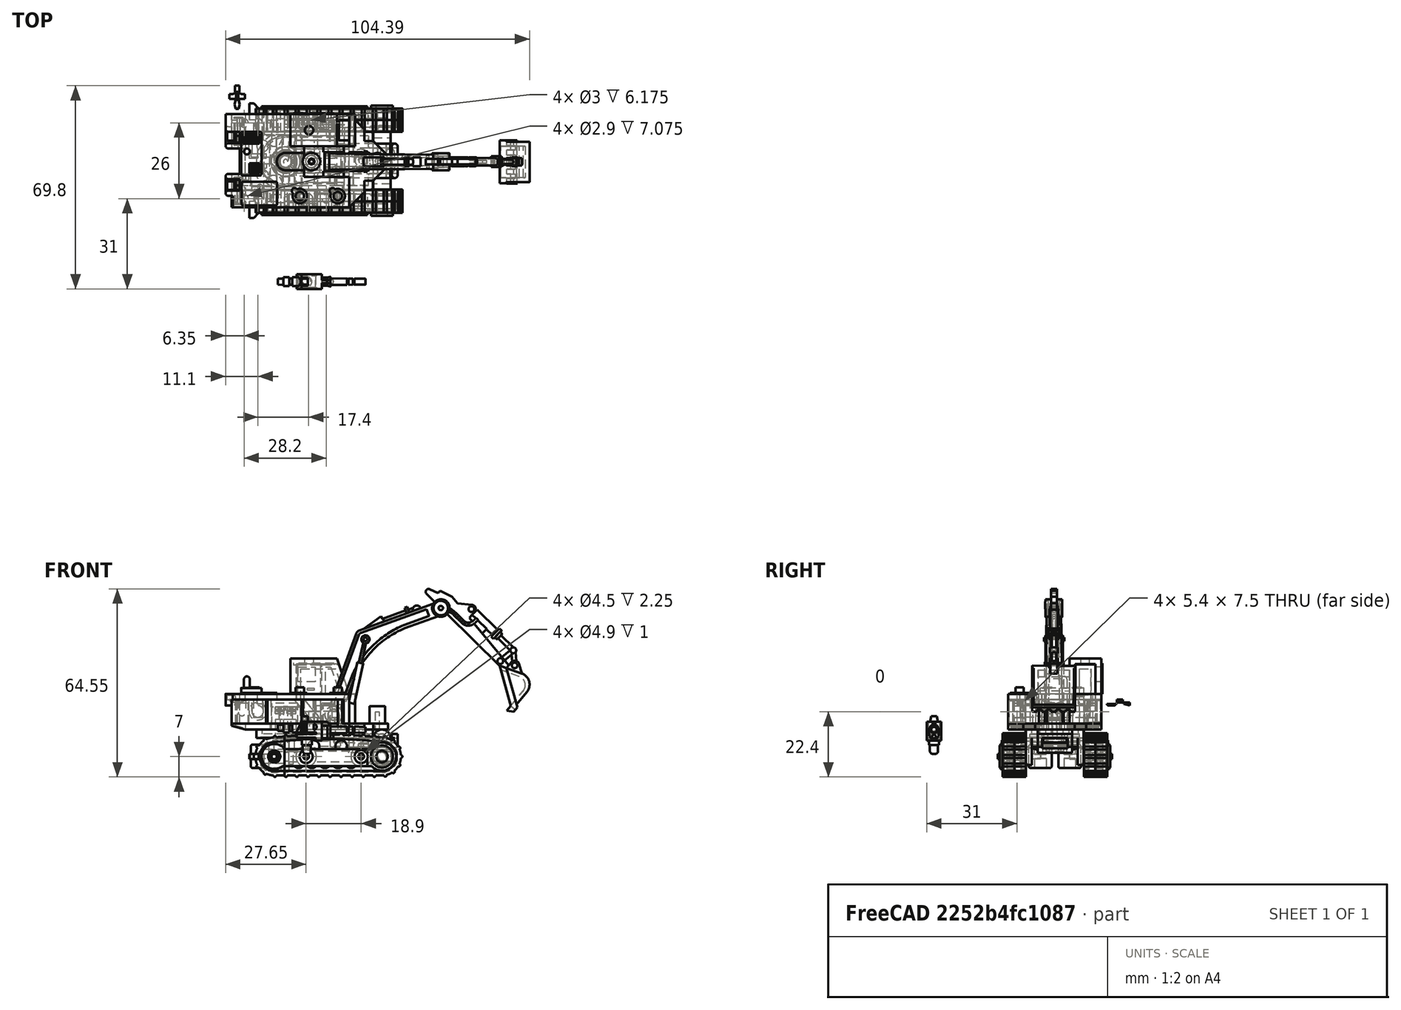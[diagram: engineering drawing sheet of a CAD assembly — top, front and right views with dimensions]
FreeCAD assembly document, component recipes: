
FREECAD ASSEMBLY — COMPONENT RECIPES ("Scavanger")

This assembly document has 15 components, labeled P0..P14 below (a component is one placed body or linked part). 15 of them carry a construction recipe — the FreeCAD feature program that regenerates the part from scratch, quoted from this document or its linked companion documents; the rest are supplied as boundary geometry only. No exploded tour is included for this assembly.
NOTE — document 4 of 4 of this assembly tour. The two overview renders and the header above are repeated from document 1; the component sections below continue where the previous document stopped.
COMPONENT P14 — recipe-attached ("Head", modeled in this document).
Construction recipe (the document's own serialized feature program — sketch geometry with constraints, then the solid features built on it; lengths are millimeters unless a unit is written):

FEATURE [Sketcher::SketchObject] Sketch213
  ArcFitTolerance = 1e-06
  AttachmentSupport = -> [XY_Plane011]
  FullyConstrained = true
  MakeInternals = false
  MapMode = 5
  sketch-geometry (4):
    g0: LineSegment StartX=0 StartY=0 StartZ=0 EndX=7.9 EndY=0 EndZ=0
    g1: LineSegment StartX=7.9 StartY=0 StartZ=0 EndX=7.9 EndY=9.8 EndZ=0
    g2: LineSegment StartX=7.9 StartY=9.8 StartZ=0 EndX=0 EndY=9.8 EndZ=0
    g3: LineSegment StartX=0 StartY=9.8 StartZ=0 EndX=0 EndY=0 EndZ=0
  constraints (11):
    c: Coincident(g0,g1)
    c: Coincident(g1,g2)
    c: Coincident(g2,g3)
    c: Coincident(g3,g0)
    c: Horizontal(g0)
    c: Horizontal(g2)
    c: Vertical(g1)
    c: Vertical(g3)
    c: Coincident(g0,g-1)
    c: DistanceX(g0,g0) = 7.9
    c: DistanceY(g1,g1) = 9.8
FEATURE [PartDesign::Pad] Pad137
  Direction = (0,0,1)
  Length = 2.75
  Length2 = 10
  Profile = -> Sketch213
  ReferenceAxis = -> Sketch213 [N_Axis]
  Refine = true
  Suppressed = false
  Type = 0
FEATURE [Sketcher::SketchObject] Sketch214
  ArcFitTolerance = 1e-06
  AttachmentSupport = -> [Pad137]
  ExternalGeometry = -> [Pad137]
  FullyConstrained = true
  MakeInternals = false
  MapMode = 5
  Placement = pos=(0,0,0) rot=(1,0,0;3.14159rad)
  sketch-geometry (4):
    g0: LineSegment StartX=0 StartY=0 StartZ=0 EndX=0 EndY=-1.4 EndZ=0
    g1: LineSegment StartX=0 StartY=-1.4 StartZ=0 EndX=7.9 EndY=-1.4 EndZ=0
    g2: LineSegment StartX=7.9 StartY=-1.4 StartZ=0 EndX=7.9 EndY=0 EndZ=0
    g3: LineSegment StartX=7.9 StartY=0 StartZ=0 EndX=0 EndY=0 EndZ=0
  constraints (11):
    c: Coincident(g0,g1)
    c: Coincident(g1,g2)
    c: Coincident(g2,g3)
    c: Coincident(g3,g0)
    c: Vertical(g0)
    c: Vertical(g2)
    c: Horizontal(g1)
    c: Horizontal(g3)
    c: Coincident(g0,g-1)
    c: PointOnObject(g1,g-3)
    c: DistanceY(g2,g2) = 1.4
FEATURE [PartDesign::Pad] Pad138
  BaseFeature = -> Pad137
  Direction = (0,0,-1)
  Length = 2
  Length2 = 10
  Profile = -> Sketch214
  ReferenceAxis = -> Sketch214 [N_Axis]
  Refine = true
  Suppressed = false
  Type = 0
FEATURE [Sketcher::SketchObject] Sketch215
  ArcFitTolerance = 1e-06
  AttachmentSupport = -> [Pad138]
  ExternalGeometry = -> [Pad138]
  FullyConstrained = true
  MakeInternals = false
  MapMode = 5
  Placement = pos=(0,0,0) rot=(0.57735,-0.57735,-0.57735;2.0944rad)
  sketch-geometry (1):
    g0: Circle CenterX=-8.5 CenterY=0 CenterZ=0 NormalX=0 NormalY=0 NormalZ=1 AngleXU=0 Radius=1.3
  constraints (3):
    c: Diameter(g0) = 2.6
    c: PointOnObject(g0,g-4)
    c: PointOnObject(g-4,g0)
FEATURE [PartDesign::Pad] Pad139
  BaseFeature = -> Pad138
  Direction = (-1,0,0)
  Length = 1.6
  Length2 = 10
  Profile = -> Sketch215
  ReferenceAxis = -> Sketch215 [N_Axis]
  Refine = true
  Suppressed = false
  Type = 0
FEATURE [PartDesign::Pad] Pad140
  BaseFeature = -> Pad139
  Direction = (-1,0,0)
  Length = 9.5
  Length2 = 10
  Profile = -> Sketch215
  ReferenceAxis = -> Sketch215 [N_Axis]
  Refine = true
  Reversed = true
  Suppressed = false
  Type = 0
FEATURE [Sketcher::SketchObject] Sketch216
  ArcFitTolerance = 1e-06
  AttachmentSupport = -> [Pad140]
  ExternalGeometry = -> [Pad140]
  FullyConstrained = true
  MakeInternals = false
  MapMode = 5
  Placement = pos=(0,0,0) rot=(0.57735,-0.57735,-0.57735;2.0944rad)
  sketch-geometry (4):
    g0: LineSegment StartX=-6.9 StartY=2.75 StartZ=0 EndX=-6.9 EndY=0 EndZ=0
    g1: LineSegment StartX=-6.9 StartY=0 StartZ=0 EndX=-5.4 EndY=0 EndZ=0
    g2: LineSegment StartX=-5.4 StartY=0 StartZ=0 EndX=-5.4 EndY=2.75 EndZ=0
    g3: LineSegment StartX=-5.4 StartY=2.75 StartZ=0 EndX=-6.9 EndY=2.75 EndZ=0
  constraints (12):
    c: Coincident(g0,g1)
    c: Coincident(g1,g2)
    c: Coincident(g2,g3)
    c: Coincident(g3,g0)
    c: Vertical(g0)
    c: Vertical(g2)
    c: Horizontal(g1)
    c: Horizontal(g3)
    c: PointOnObject(g0,g-3)
    c: PointOnObject(g1,g-4)
    c: DistanceX(g1,g1) = 1.5
    c: DistanceX(g-3,g0) = 2.9
FEATURE [PartDesign::Pad] Pad141
  BaseFeature = -> Pad140
  Direction = (-1,0,0)
  Length = 0.45
  Length2 = 10
  Profile = -> Sketch216
  ReferenceAxis = -> Sketch216 [N_Axis]
  Refine = true
  Suppressed = false
  Type = 0
FEATURE [Sketcher::SketchObject] Sketch217
  ArcFitTolerance = 1e-06
  AttachmentSupport = -> [Pad141]
  ExternalGeometry = -> [Pad141]
  FullyConstrained = true
  MakeInternals = false
  MapMode = 5
  Placement = pos=(7.9,0,0) rot=(0.57735,0.57735,0.57735;2.0944rad)
  sketch-geometry (4):
    g0: LineSegment StartX=5.4 StartY=2.75 StartZ=0 EndX=5.4 EndY=0 EndZ=0
    g1: LineSegment StartX=5.4 StartY=0 StartZ=0 EndX=6.9 EndY=0 EndZ=0
    g2: LineSegment StartX=6.9 StartY=0 StartZ=0 EndX=6.9 EndY=2.75 EndZ=0
    g3: LineSegment StartX=6.9 StartY=2.75 StartZ=0 EndX=5.4 EndY=2.75 EndZ=0
  constraints (10):
    c: Coincident(g0,g1)
    c: Coincident(g1,g2)
    c: Coincident(g2,g3)
    c: Coincident(g3,g0)
    c: Vertical(g0)
    c: Vertical(g2)
    c: Horizontal(g1)
    c: Horizontal(g3)
    c: Coincident(g0,g-3)
    c: Coincident(g1,g-4)
FEATURE [PartDesign::Pad] Pad142
  BaseFeature = -> Pad141
  Direction = (1,0,0)
  Length = 0.45
  Length2 = 10
  Profile = -> Sketch217
  ReferenceAxis = -> Sketch217 [N_Axis]
  Refine = true
  Suppressed = false
  Type = 0
FEATURE [PartDesign::Chamfer] Chamfer003
  Angle = 45
  Base = -> Pad142 [Edge47,Edge45,Edge16,Edge18]
  BaseFeature = -> Pad142
  ChamferType = 0
  FlipDirection = false
  Refine = true
  Size = 0.4
  Size2 = 1
  SupportTransform = false
  Suppressed = false
  UseAllEdges = false
FEATURE [Sketcher::SketchObject] Sketch218
  ArcFitTolerance = 1e-06
  AttachmentSupport = -> [Chamfer003]
  ExternalGeometry = -> [Chamfer003]
  FullyConstrained = true
  MakeInternals = false
  MapMode = 5
  Placement = pos=(0,0,2.75) rot=(0,0,1;0rad)
  sketch-geometry (1):
    g0: Circle CenterX=3.95 CenterY=4.9 CenterZ=0 NormalX=0 NormalY=0 NormalZ=1 AngleXU=0 Radius=2.45
  constraints (5):
    c: Diameter(g0) = 4.9
    c: DistanceX(g-3,g-3) = 7.9
    c: DistanceY(g-4,g-3) = 9.8
    c: DistanceX(g0,g-4) = 3.95
    c: DistanceY(g-4,g0) = 4.9
FEATURE [PartDesign::Pocket] Pocket098
  BaseFeature = -> Chamfer003
  Direction = (0,0,-1)
  Length = 1.7
  Length2 = 5
  Profile = -> Sketch218
  ReferenceAxis = -> Sketch218 [N_Axis]
  Refine = true
  Suppressed = false
  Type = 0
FEATURE [Sketcher::SketchObject] Sketch219
  ArcFitTolerance = 1e-06
  AttachmentOffset = pos=(0,0,-1) rot=(0,0,1;0rad)
  AttachmentSupport = -> [Pocket098]
  ExternalGeometry = -> [Pocket098]
  FullyConstrained = true
  MakeInternals = false
  MapMode = 5
  Placement = pos=(1,0,0) rot=(0.57735,-0.57735,-0.57735;2.0944rad)
  sketch-geometry (5):
    g0: ArcOfCircle CenterX=-7.19261 CenterY=0.257783 CenterZ=0 NormalX=0 NormalY=0 NormalZ=1 AngleXU=0 Radius=4.5 StartAngle=5.75759 EndAngle=6.22587
    g1: LineSegment [constr] StartX=-1.4 StartY=-2 StartZ=0 EndX=-3.3 EndY=-2 EndZ=0
    g2: LineSegment StartX=-3.3 StartY=-2 StartZ=0 EndX=-5.26914 EndY=-1.65 EndZ=0
    g3: ArcOfCircle CenterX=-12.6824 CenterY=-0.512926 CenterZ=0 NormalX=0 NormalY=0 NormalZ=1 AngleXU=0 Radius=7.5 StartAngle=6.13099 EndAngle=6.35163
    g4: LineSegment StartX=-5.2 StartY=-1.3e-15 StartZ=0 EndX=-2.7 EndY=1.6e-15 EndZ=0
  constraints (16):
    c: PointOnObject(g0,g-3)
    c: DistanceX(g0,g-3) = 1.3
    c: Coincident(g1,g-4)
    c: Coincident(g1,g0)
    c: Horizontal(g1)
    c: Coincident(g2,g0)
    c: Coincident(g3,g2)
    c: PointOnObject(g3,g-3)
    c: Coincident(g4,g3)
    c: Coincident(g4,g0)
    c: DistanceX(g3,g0) = 2.5
    c: Distance(g2) = 2
    c: DistanceX(g0,g0) = 0.6
    c: Radius(g0) = 4.5
    c: Radius(g3) = 7.5
    c: DistanceY(g0,g2) = 0.35
FEATURE [PartDesign::Pad] Pad143
  BaseFeature = -> Pocket098
  Direction = (-1,0,0)
  Length = 5.9
  Length2 = 10
  Profile = -> Sketch219
  ReferenceAxis = -> Sketch219 [N_Axis]
  Refine = true
  Reversed = true
  Suppressed = false
  Type = 0
FEATURE [Sketcher::SketchObject] Sketch220
  ArcFitTolerance = 1e-06
  AttachmentSupport = -> [Pad143]
  ExternalGeometry = -> [Pad143]
  FullyConstrained = true
  MakeInternals = false
  MapMode = 5
  Placement = pos=(1,0,0) rot=(0.57735,-0.57735,-0.57735;2.0944rad)
  sketch-geometry (4):
    g0: ArcOfCircle CenterX=-7.19261 CenterY=0.257783 CenterZ=0 NormalX=0 NormalY=0 NormalZ=1 AngleXU=0 Radius=4.5 StartAngle=5.85761 EndAngle=6.22587
    g1: LineSegment StartX=-3.094 StartY=-1.6 StartZ=0 EndX=-1.6 EndY=-0.737441 EndZ=0
    g2: LineSegment StartX=-1.6 StartY=-0.737441 StartZ=0 EndX=-1.6 EndY=0 EndZ=0
    g3: LineSegment StartX=-2.7 StartY=1.6e-15 StartZ=0 EndX=-1.6 EndY=0 EndZ=0
  constraints (11):
    c: PointOnObject(g0,g-3)
    c: Tangent(g0,g-3) = -1.5708
    c: DistanceY(g0,g0) = 1.6
    c: Coincident(g1,g0)
    c: Coincident(g2,g1)
    c: PointOnObject(g2,g-4)
    c: Vertical(g2)
    c: Coincident(g3,g0)
    c: Coincident(g3,g2)
    c: DistanceX(g3,g3) = 1.1
    c: Angle(g2,g1) = 2.0944
FEATURE [PartDesign::Pad] Pad144
  BaseFeature = -> Pad143
  Direction = (-1,0,0)
  Length = 5.9
  Length2 = 10
  Profile = -> Sketch220
  ReferenceAxis = -> Sketch220 [N_Axis]
  Refine = true
  Reversed = true
  Suppressed = false
  Type = 0
FEATURE [Sketcher::SketchObject] Sketch221
  ArcFitTolerance = 1e-06
  AttachmentSupport = -> [Pad144]
  ExternalGeometry = -> [Pad144]
  FullyConstrained = true
  MakeInternals = false
  MapMode = 5
  Placement = pos=(0,0,-2) rot=(1,0,0;3.14159rad)
  sketch-geometry (4):
    g0: LineSegment StartX=2.5 StartY=-1.6 StartZ=0 EndX=2.5 EndY=-3.094 EndZ=0
    g1: LineSegment StartX=2.5 StartY=-3.094 StartZ=0 EndX=5.4 EndY=-3.094 EndZ=0
    g2: LineSegment StartX=5.4 StartY=-3.094 StartZ=0 EndX=5.4 EndY=-1.6 EndZ=0
    g3: LineSegment StartX=5.4 StartY=-1.6 StartZ=0 EndX=2.5 EndY=-1.6 EndZ=0
  constraints (12):
    c: Coincident(g0,g1)
    c: Coincident(g1,g2)
    c: Coincident(g2,g3)
    c: Coincident(g3,g0)
    c: Vertical(g0)
    c: Vertical(g2)
    c: Horizontal(g1)
    c: Horizontal(g3)
    c: PointOnObject(g0,g-5)
    c: PointOnObject(g1,g-6)
    c: DistanceX(g-5,g0) = 1.5
    c: DistanceX(g2,g-5) = 1.5
FEATURE [PartDesign::Pocket] Pocket099
  BaseFeature = -> Pad144
  Direction = (0,0,1)
  Length = 2
  Length2 = 5
  Profile = -> Sketch221
  ReferenceAxis = -> Sketch221 [N_Axis]
  Refine = true
  Suppressed = false
  Type = 0
FEATURE [Sketcher::SketchObject] Sketch222
  ArcFitTolerance = 1e-06
  AttachmentSupport = -> [Pocket099]
  ExternalGeometry = -> [Pocket099]
  FullyConstrained = true
  MakeInternals = false
  MapMode = 5
  Placement = pos=(0,0,-2) rot=(1,0,0;3.14159rad)
  sketch-geometry (9):
    g0: LineSegment StartX=3.2 StartY=-1.6 StartZ=0 EndX=4.7 EndY=-1.6 EndZ=0
    g1: LineSegment StartX=4.7 StartY=-1.6 StartZ=0 EndX=5.075 EndY=-3.3 EndZ=0
    g2: LineSegment StartX=5.075 StartY=-3.3 StartZ=0 EndX=4.7 EndY=-5.26914 EndZ=0
    g3: LineSegment StartX=4.7 StartY=-5.26914 StartZ=0 EndX=3.2 EndY=-5.26914 EndZ=0
    g4: LineSegment StartX=3.2 StartY=-5.26914 StartZ=0 EndX=2.825 EndY=-3.3 EndZ=0
    g5: LineSegment StartX=2.825 StartY=-3.3 StartZ=0 EndX=3.2 EndY=-1.6 EndZ=0
    g6: LineSegment [constr] StartX=3.2 StartY=-1.6 StartZ=0 EndX=3.2 EndY=-5.26914 EndZ=0
    g7: LineSegment [constr] StartX=4.7 StartY=-1.6 StartZ=0 EndX=4.7 EndY=-5.26914 EndZ=0
    g8: LineSegment [constr] StartX=3.2 StartY=-1.6 StartZ=0 EndX=2.5 EndY=-1.6 EndZ=0
  constraints (26):
    c: Horizontal(g0)
    c: Coincident(g1,g0)
    c: PointOnObject(g1,g-8)
    c: Coincident(g2,g1)
    c: PointOnObject(g2,g-3)
    c: Coincident(g3,g2)
    c: PointOnObject(g3,g-3)
    c: Coincident(g4,g3)
    c: PointOnObject(g4,g-8)
    c: Coincident(g5,g4)
    c: Coincident(g5,g0)
    c: DistanceX(g0,g0) = 1.5
    c: DistanceX(g3,g3) = 1.5
    c: Coincident(g6,g0)
    c: Coincident(g6,g3)
    c: Vertical(g6)
    c: Coincident(g7,g0)
    c: Coincident(g7,g2)
    c: Coincident(g8,g0)
    c: Coincident(g8,g-6)
    c: Horizontal(g8)
    c: DistanceX(g4,g1) = 2.25
    c: DistanceX(g8,g-5) = 2.9
    c: DistanceX(g8,g0) = 0.7
    c: DistanceX(g-7,g4) = 0.325
    c: DistanceX(g1,g-7) = 0.325
FEATURE [PartDesign::Pad] Pad145
  BaseFeature = -> Pocket099
  Direction = (0,0,-1)
  Length = 2
  Length2 = 10
  Profile = -> Sketch222
  ReferenceAxis = -> Sketch222 [N_Axis]
  Refine = true
  Reversed = true
  Suppressed = false
  Type = 0
FEATURE [Sketcher::SketchObject] Sketch223
  ArcFitTolerance = 1e-06
  AttachmentSupport = -> [Pad145]
  ExternalGeometry = -> [Pad145]
  FullyConstrained = true
  MakeInternals = false
  MapMode = 5
  Placement = pos=(6.9,0,0) rot=(0.57735,0.57735,0.57735;2.0944rad)
  sketch-geometry (3):
    g0: LineSegment StartX=5.26914 StartY=-1.65 StartZ=0 EndX=5.26914 EndY=0 EndZ=0
    g1: LineSegment StartX=5.26914 StartY=0 StartZ=0 EndX=5.2 EndY=-1.3e-15 EndZ=0
    g2: ArcOfCircle CenterX=12.6825 CenterY=-0.512923 CenterZ=0 NormalX=0 NormalY=0 NormalZ=1 AngleXU=0 Radius=7.50006 StartAngle=3.07315 EndAngle=3.29379
  constraints (7):
    c: Coincident(g0,g-5)
    c: Coincident(g0,g-3)
    c: Coincident(g1,g0)
    c: Coincident(g1,g-5)
    c: Coincident(g2,g1)
    c: Coincident(g2,g0)
    c: Tangent(g2,g-5)
FEATURE [PartDesign::Pocket] Pocket100
  BaseFeature = -> Pad145
  Direction = (-1,0,0)
  Length = 5
  Length2 = 5
  Profile = -> Sketch223
  ReferenceAxis = -> Sketch223 [N_Axis]
  Refine = true
  Suppressed = false
  Type = 0
FEATURE [Sketcher::SketchObject] Sketch224
  ArcFitTolerance = 1e-06
  AttachmentSupport = -> [Pocket100]
  ExternalGeometry = -> [Pocket100]
  FullyConstrained = true
  MakeInternals = false
  MapMode = 5
  Placement = pos=(0,0,-2) rot=(1,0,0;3.14159rad)
  sketch-geometry (8):
    g0: LineSegment StartX=3.35588 StartY=-1.8 StartZ=0 EndX=4.54412 EndY=-1.8 EndZ=0
    g1: LineSegment StartX=4.54412 StartY=-1.8 StartZ=0 EndX=4.875 EndY=-3.3 EndZ=0
    g2: LineSegment StartX=4.875 StartY=-3.3 StartZ=0 EndX=4.53809 EndY=-5.06914 EndZ=0
    g3: LineSegment StartX=4.53809 StartY=-5.06914 StartZ=0 EndX=3.36191 EndY=-5.06914 EndZ=0
    g4: LineSegment StartX=3.36191 StartY=-5.06914 StartZ=0 EndX=3.025 EndY=-3.3 EndZ=0
    g5: LineSegment StartX=3.025 StartY=-3.3 StartZ=0 EndX=3.35588 EndY=-1.8 EndZ=0
    g6: LineSegment [constr] StartX=3.025 StartY=-3.3 StartZ=0 EndX=2.825 EndY=-3.3 EndZ=0
    g7: LineSegment [constr] StartX=4.875 StartY=-3.3 StartZ=0 EndX=5.075 EndY=-3.3 EndZ=0
  constraints (22):
    c: Horizontal(g0)
    c: Coincident(g1,g0)
    c: Coincident(g2,g1)
    c: Coincident(g3,g2)
    c: Horizontal(g3)
    c: Coincident(g4,g3)
    c: Coincident(g5,g4)
    c: Coincident(g5,g0)
    c: Parallel(g5,g-7)
    c: Parallel(g2,g-5)
    c: Parallel(g1,g-4)
    c: Parallel(g4,g-6)
    c: DistanceY(g0,g-7) = 0.2
    c: DistanceY(g-6,g3) = 0.2
    c: Coincident(g6,g4)
    c: Coincident(g6,g-7)
    c: Coincident(g7,g1)
    c: Coincident(g7,g-5)
    c: Horizontal(g6)
    c: Horizontal(g7)
    c: DistanceX(g6,g6) = 0.2
    c: DistanceX(g7,g7) = 0.2
FEATURE [PartDesign::Pocket] Pocket101
  BaseFeature = -> Pocket100
  Direction = (0,0,1)
  Length = 0.5
  Length2 = 5
  Profile = -> Sketch224
  ReferenceAxis = -> Sketch224 [N_Axis]
  Refine = true
  Suppressed = false
  Type = 0
FEATURE [Sketcher::SketchObject] Sketch225
  ArcFitTolerance = 1e-06
  AttachmentSupport = -> [Pocket101]
  ExternalGeometry = -> [Pocket101]
  FullyConstrained = true
  MakeInternals = false
  MapMode = 5
  Placement = pos=(0,0,-2) rot=(1,0,0;3.14159rad)
  sketch-geometry (4):
    g0: LineSegment StartX=3.2 StartY=-7.2 StartZ=0 EndX=3.2 EndY=-9.8 EndZ=0
    g1: LineSegment StartX=3.2 StartY=-9.8 StartZ=0 EndX=4.7 EndY=-9.8 EndZ=0
    g2: LineSegment StartX=4.7 StartY=-9.8 StartZ=0 EndX=4.7 EndY=-7.2 EndZ=0
    g3: LineSegment StartX=4.7 StartY=-7.2 StartZ=0 EndX=3.2 EndY=-7.2 EndZ=0
  constraints (13):
    c: Coincident(g0,g1)
    c: Coincident(g1,g2)
    c: Coincident(g2,g3)
    c: Coincident(g3,g0)
    c: Vertical(g0)
    c: Vertical(g2)
    c: Horizontal(g1)
    c: Horizontal(g3)
    c: PointOnObject(g0,g-3)
    c: PointOnObject(g1,g-4)
    c: DistanceX(g3,g3) = 1.5
    c: DistanceX(g-4,g-4) = 7.9
    c: DistanceX(g-3,g0) = 3.2
FEATURE [PartDesign::Pocket] Pocket102
  BaseFeature = -> Pocket101
  Direction = (0,0,1)
  Length = 1
  Length2 = 5
  Profile = -> Sketch225
  ReferenceAxis = -> Sketch225 [N_Axis]
  Refine = true
  Suppressed = false
  Type = 0
FEATURE [Sketcher::SketchObject] Sketch226
  ArcFitTolerance = 1e-06
  AttachmentSupport = -> [Pocket102]
  ExternalGeometry = -> [Pocket102]
  FullyConstrained = true
  MakeInternals = false
  MapMode = 5
  Placement = pos=(0,0,-2) rot=(1,0,0;3.14159rad)
  sketch-geometry (8):
    g0: LineSegment StartX=1.15 StartY=-7.2 StartZ=0 EndX=1.15 EndY=-9.8 EndZ=0
    g1: LineSegment StartX=1.15 StartY=-9.8 StartZ=0 EndX=1.95 EndY=-9.8 EndZ=0
    g2: LineSegment StartX=1.95 StartY=-9.8 StartZ=0 EndX=1.95 EndY=-7.2 EndZ=0
    g3: LineSegment StartX=1.95 StartY=-7.2 StartZ=0 EndX=1.15 EndY=-7.2 EndZ=0
    g4: LineSegment StartX=5.95 StartY=-7.2 StartZ=0 EndX=5.95 EndY=-9.8 EndZ=0
    g5: LineSegment StartX=5.95 StartY=-9.8 StartZ=0 EndX=6.75 EndY=-9.8 EndZ=0
    g6: LineSegment StartX=6.75 StartY=-9.8 StartZ=0 EndX=6.75 EndY=-7.2 EndZ=0
    g7: LineSegment StartX=6.75 StartY=-7.2 StartZ=0 EndX=5.95 EndY=-7.2 EndZ=0
  constraints (25):
    c: Coincident(g0,g1)
    c: Coincident(g1,g2)
    c: Coincident(g2,g3)
    c: Coincident(g3,g0)
    c: Vertical(g0)
    c: Vertical(g2)
    c: Horizontal(g1)
    c: Horizontal(g3)
    c: PointOnObject(g0,g-3)
    c: PointOnObject(g1,g-4)
    c: Coincident(g4,g5)
    c: Coincident(g5,g6)
    c: Coincident(g6,g7)
    c: Coincident(g7,g4)
    c: Vertical(g4)
    c: Vertical(g6)
    c: Horizontal(g5)
    c: Horizontal(g7)
    c: PointOnObject(g4,g-3)
    c: PointOnObject(g5,g-4)
    c: DistanceX(g3,g3) = 0.8
    c: DistanceX(g7,g7) = 0.8
    c: DistanceX(g-4,g-4) = 7.9
    c: DistanceX(g-4,g0) = 1.15
    c: DistanceX(g5,g-4) = 1.15
FEATURE [PartDesign::Pad] Pad146
  BaseFeature = -> Pocket102
  Direction = (0,0,-1)
  Length = 2
  Length2 = 10
  Profile = -> Sketch226
  ReferenceAxis = -> Sketch226 [N_Axis]
  Refine = true
  Reversed = true
  Suppressed = false
  Type = 0
FEATURE [Sketcher::SketchObject] Sketch227
  ArcFitTolerance = 1e-06
  AttachmentSupport = -> [Pad146]
  ExternalGeometry = -> [Pad146]
  FullyConstrained = true
  MakeInternals = false
  MapMode = 5
  Placement = pos=(0,0,-2) rot=(1,0,0;3.14159rad)
  sketch-geometry (4):
    g0: LineSegment StartX=3.2 StartY=-7.66934 StartZ=0 EndX=2.35 EndY=-7.2 EndZ=0
    g1: LineSegment StartX=2.35 StartY=-7.2 StartZ=0 EndX=5.55 EndY=-7.2 EndZ=0
    g2: LineSegment StartX=5.55 StartY=-7.2 StartZ=0 EndX=4.7 EndY=-7.66934 EndZ=0
    g3: LineSegment StartX=4.7 StartY=-7.66934 StartZ=0 EndX=3.2 EndY=-7.66934 EndZ=0
  constraints (10):
    c: Coincident(g0,g-4)
    c: PointOnObject(g0,g-3)
    c: Coincident(g1,g0)
    c: PointOnObject(g1,g-3)
    c: Coincident(g2,g1)
    c: Coincident(g2,g-4)
    c: Coincident(g3,g2)
    c: Coincident(g3,g0)
    c: DistanceX(g-3,g0) = 0.4
    c: DistanceX(g1,g-3) = 0.4
FEATURE [PartDesign::Pocket] Pocket103
  BaseFeature = -> Pad146
  Direction = (0,0,1)
  Length = 2
  Length2 = 5
  Profile = -> Sketch227
  ReferenceAxis = -> Sketch227 [N_Axis]
  Refine = true
  Suppressed = false
  Type = 0
FEATURE [Sketcher::SketchObject] Sketch228
  ArcFitTolerance = 1e-06
  AttachmentSupport = -> [Pocket103]
  ExternalGeometry = -> [Pocket103]
  FullyConstrained = true
  MakeInternals = false
  MapMode = 5
  Placement = pos=(0,0,0) rot=(1,0,0;3.14159rad)
  sketch-geometry (16):
    g0: LineSegment StartX=3.27732 StartY=-7.36934 StartZ=0 EndX=2.42732 EndY=-6.9 EndZ=0
    g1: LineSegment StartX=3.27732 StartY=-7.36934 StartZ=0 EndX=4.62268 EndY=-7.36934 EndZ=0
    g2: LineSegment StartX=4.62268 StartY=-7.36934 StartZ=0 EndX=5.47268 EndY=-6.9 EndZ=0
    g3: LineSegment StartX=5.47268 StartY=-6.9 StartZ=0 EndX=6.9 EndY=-6.9 EndZ=0
    g4: LineSegment StartX=6.9 StartY=-6.9 StartZ=0 EndX=6.9 EndY=-7.2 EndZ=0
    g5: LineSegment StartX=6.9 StartY=-7.2 StartZ=0 EndX=5.55 EndY=-7.2 EndZ=0
    g6: LineSegment StartX=5.55 StartY=-7.2 StartZ=0 EndX=4.7 EndY=-7.66934 EndZ=0
    g7: LineSegment StartX=4.7 StartY=-7.66934 StartZ=0 EndX=3.2 EndY=-7.66934 EndZ=0
    g8: LineSegment StartX=3.2 StartY=-7.66934 StartZ=0 EndX=2.35 EndY=-7.2 EndZ=0
    g9: LineSegment StartX=2.35 StartY=-7.2 StartZ=0 EndX=1 EndY=-7.2 EndZ=0
    g10: LineSegment StartX=1 StartY=-7.2 StartZ=0 EndX=1 EndY=-6.9 EndZ=0
    g11: LineSegment StartX=2.42732 StartY=-6.9 StartZ=0 EndX=1 EndY=-6.9 EndZ=0
    g12: LineSegment [constr] StartX=1 StartY=-5.26914 StartZ=0 EndX=1 EndY=-6.9 EndZ=0
    g13: LineSegment [constr] StartX=6.9 StartY=-5.26914 StartZ=0 EndX=6.9 EndY=-6.9 EndZ=0
    g14: LineSegment [constr] StartX=2.78771 StartY=-7.44169 StartZ=0 EndX=2.93272 EndY=-7.17906 EndZ=0
    g15: LineSegment [constr] StartX=5.11229 StartY=-7.44169 StartZ=0 EndX=4.96728 EndY=-7.17906 EndZ=0
  constraints (44):
    c: Coincident(g1,g0)
    c: Horizontal(g1)
    c: Coincident(g2,g1)
    c: Coincident(g3,g2)
    c: Horizontal(g3)
    c: Coincident(g4,g3)
    c: PointOnObject(g4,g-11)
    c: Coincident(g5,g4)
    c: Coincident(g5,g-6)
    c: Coincident(g6,g5)
    c: Coincident(g6,g-7)
    c: Coincident(g7,g6)
    c: Coincident(g7,g-7)
    c: Coincident(g8,g7)
    c: Coincident(g8,g-8)
    c: Coincident(g9,g8)
    c: PointOnObject(g9,g-10)
    c: Coincident(g10,g9)
    c: Vertical(g10)
    c: Coincident(g11,g0)
    c: Coincident(g11,g10)
    c: Horizontal(g11)
    c: Parallel(g0,g8)
    c: Parallel(g2,g6)
    c: Vertical(g4)
    c: Coincident(g12,g-3)
    c: Coincident(g12,g10)
    c: Vertical(g12)
    c: Coincident(g13,g-4)
    c: Coincident(g13,g3)
    c: Vertical(g13)
    c: DistanceY(g4,g4) = 0.3
    c: DistanceY(g10,g10) = 0.3
    c: DistanceY(g7,g0) = 0.3
    c: Perpendicular(g14,g8)
    c: Distance(g14) = 0.3
    c: PointOnObject(g14,g8)
    c: PointOnObject(g14,g0)
    c: Distance(g14,g8) = 0.5
    c: PointOnObject(g15,g6)
    c: PointOnObject(g15,g2)
    c: Perpendicular(g15,g6)
    c: Distance(g5,g15) = 0.5
    c: Distance(g15) = 0.3
FEATURE [PartDesign::Pad] Pad147
  BaseFeature = -> Pocket103
  Direction = (0,0,-1)
  Length = 1.5
  Length2 = 10
  Profile = -> Sketch228
  ReferenceAxis = -> Sketch228 [N_Axis]
  Refine = true
  Suppressed = false
  Type = 0
FEATURE [Sketcher::SketchObject] Sketch229
  ArcFitTolerance = 1e-06
  AttachmentSupport = -> [Pad147]
  ExternalGeometry = -> [Pad147]
  FullyConstrained = true
  MakeInternals = false
  MapMode = 5
  Placement = pos=(0,6.9,0) rot=(1,0,0;1.5708rad)
  sketch-geometry (6):
    g0: LineSegment StartX=6.9 StartY=-1e-16 StartZ=0 EndX=6.9 EndY=-1.5 EndZ=0
    g1: LineSegment StartX=6.9 StartY=-1.5 StartZ=0 EndX=5.47268 EndY=-1.5 EndZ=0
    g2: LineSegment StartX=5.47268 StartY=-1.5 StartZ=0 EndX=6.9 EndY=2e-16 EndZ=0
    g3: LineSegment StartX=2.42732 StartY=-1.5 StartZ=0 EndX=1 EndY=0 EndZ=0
    g4: LineSegment StartX=2.42732 StartY=-1.5 StartZ=0 EndX=1 EndY=-1.5 EndZ=0
    g5: LineSegment StartX=1 StartY=-1.5 StartZ=0 EndX=1 EndY=0 EndZ=0
  constraints (12):
    c: Coincident(g0,g-6)
    c: Coincident(g0,g-6)
    c: Coincident(g1,g0)
    c: Coincident(g1,g-5)
    c: Coincident(g2,g1)
    c: Coincident(g2,g0)
    c: Coincident(g3,g-3)
    c: Coincident(g3,g-4)
    c: Coincident(g4,g3)
    c: Coincident(g4,g-4)
    c: Coincident(g5,g4)
    c: Coincident(g5,g3)
FEATURE [PartDesign::Pocket] Pocket104
  BaseFeature = -> Pad147
  Direction = (0,1,-2e-16)
  Length = 0.3
  Length2 = 5
  Profile = -> Sketch229
  ReferenceAxis = -> Sketch229 [N_Axis]
  Refine = true
  Suppressed = false
  Type = 0
FEATURE [PartDesign::Pocket] Pocket105
  BaseFeature = -> Pocket104
  Direction = (0,1,0)
  Length = 0.1
  Length2 = 5
  Profile = -> Pocket104 [Face63]
  Refine = true
  Suppressed = false
  Type = 0
FEATURE [PartDesign::Pocket] Pocket106
  BaseFeature = -> Pocket105
  Direction = (0,1,0)
  Length = 0.1
  Length2 = 5
  Profile = -> Pocket105 [Face41]
  Refine = true
  Suppressed = false
  Type = 0
FEATURE [Sketcher::SketchObject] Sketch230
  ArcFitTolerance = 1e-06
  AttachmentSupport = -> [Pocket106]
  ExternalGeometry = -> [Pocket106]
  FullyConstrained = true
  MakeInternals = false
  MapMode = 5
  Placement = pos=(0,0,-1.5) rot=(1,0,0;3.14159rad)
  sketch-geometry (6):
    g0: LineSegment StartX=4.325 StartY=-7.36934 StartZ=0 EndX=4.325 EndY=-5.76934 EndZ=0
    g1: LineSegment StartX=4.325 StartY=-5.76934 StartZ=0 EndX=3.575 EndY=-5.76934 EndZ=0
    g2: LineSegment StartX=3.575 StartY=-5.76934 StartZ=0 EndX=3.575 EndY=-7.36934 EndZ=0
    g3: LineSegment StartX=3.575 StartY=-7.36934 StartZ=0 EndX=4.325 EndY=-7.36934 EndZ=0
    g4: LineSegment [constr] StartX=3.95 StartY=-5.76934 StartZ=0 EndX=3.95 EndY=-7.36934 EndZ=0
    g5: LineSegment [constr] StartX=3.95 StartY=-7.36934 StartZ=0 EndX=3.95 EndY=-7.66934 EndZ=0
  constraints (17):
    c: Coincident(g0,g1)
    c: Coincident(g1,g2)
    c: Coincident(g2,g3)
    c: Coincident(g3,g0)
    c: Vertical(g0)
    c: Vertical(g2)
    c: Horizontal(g1)
    c: Horizontal(g3)
    c: PointOnObject(g0,g-3)
    c: DistanceX(g1,g1) = 0.75
    c: DistanceX(g-3,g-3) = 1.34536
    c: Symmetric(g1,g1,g4)
    c: Symmetric(g3,g3,g4)
    c: Coincident(g5,g4)
    c: Symmetric(g-4,g-4,g5)
    c: Vertical(g5)
    c: DistanceY(g0,g0) = 1.6
FEATURE [PartDesign::Pad] Pad148
  BaseFeature = -> Pocket106
  Direction = (0,0,-1)
  Length = 1.5
  Length2 = 10
  Profile = -> Sketch230
  ReferenceAxis = -> Sketch230 [N_Axis]
  Refine = true
  Reversed = true
  Suppressed = false
  Type = 0
FEATURE [Sketcher::SketchObject] Sketch231
  ArcFitTolerance = 1e-06
  AttachmentSupport = -> [Pad148]
  ExternalGeometry = -> [Pad148]
  FullyConstrained = true
  MakeInternals = false
  MapMode = 5
  Placement = pos=(4.325,0,0) rot=(0.57735,0.57735,0.57735;2.0944rad)
  sketch-geometry (3):
    g0: LineSegment StartX=6.9 StartY=-1.5 StartZ=0 EndX=5.76934 EndY=-1 EndZ=0
    g1: LineSegment StartX=5.76934 StartY=-1 StartZ=0 EndX=5.76934 EndY=-1.5 EndZ=0
    g2: LineSegment StartX=6.9 StartY=-1.5 StartZ=0 EndX=5.76934 EndY=-1.5 EndZ=0
  constraints (7):
    c: Coincident(g0,g-5)
    c: PointOnObject(g0,g-4)
    c: Coincident(g1,g0)
    c: Coincident(g1,g-4)
    c: Coincident(g2,g0)
    c: Coincident(g2,g1)
    c: DistanceY(g1,g1) = 0.5
FEATURE [PartDesign::Pocket] Pocket107
  BaseFeature = -> Pad148
  Direction = (-1,0,0)
  Length = 5
  Length2 = 5
  Profile = -> Sketch231
  ReferenceAxis = -> Sketch231 [N_Axis]
  Refine = true
  Suppressed = false
  Type = 0
FEATURE [PartDesign::SubShapeBinder] Binder005
  BindCopyOnChange = 0
  BindMode = 2
  ClaimChildren = false
  Context = -> Part [Body011.Binder005.]
  Fuse = false
  MakeFace = true
  OffsetFill = false
  OffsetIntersection = false
  OffsetJoinType = 0
  OffsetOpenResult = false
  PartialLoad = false
  Refine = true
  Relative = true
  _Version = 2
FEATURE [Sketcher::SketchObject] Sketch232
  ArcFitTolerance = 1e-06
  AttachmentSupport = -> [Binder005]
  ExternalGeometry = -> [Binder005]
  FullyConstrained = true
  MakeInternals = false
  MapMode = 5
  Placement = pos=(0,0,-1.5) rot=(1,0,0;3.14159rad)
  sketch-geometry (8):
    g0: LineSegment StartX=3.39485 StartY=-1.85 StartZ=0 EndX=4.50515 EndY=-1.85 EndZ=0
    g1: LineSegment StartX=4.50515 StartY=-1.85 StartZ=0 EndX=4.825 EndY=-3.3 EndZ=0
    g2: LineSegment StartX=4.825 StartY=-3.3 StartZ=0 EndX=4.49761 EndY=-5.01914 EndZ=0
    g3: LineSegment StartX=4.49761 StartY=-5.01914 StartZ=0 EndX=3.40239 EndY=-5.01914 EndZ=0
    g4: LineSegment StartX=3.40239 StartY=-5.01914 StartZ=0 EndX=3.075 EndY=-3.3 EndZ=0
    g5: LineSegment StartX=3.075 StartY=-3.3 StartZ=0 EndX=3.39485 EndY=-1.85 EndZ=0
    g6: LineSegment [constr] StartX=4.825 StartY=-3.3 StartZ=0 EndX=4.875 EndY=-3.3 EndZ=0
    g7: LineSegment [constr] StartX=3.075 StartY=-3.3 StartZ=0 EndX=3.025 EndY=-3.3 EndZ=0
  constraints (22):
    c: Horizontal(g0)
    c: Coincident(g1,g0)
    c: Coincident(g2,g1)
    c: Coincident(g3,g2)
    c: Horizontal(g3)
    c: Coincident(g4,g3)
    c: Coincident(g5,g4)
    c: Coincident(g5,g0)
    c: Parallel(g1,g-8)
    c: Parallel(g2,g-7)
    c: Parallel(g4,g-5)
    c: Parallel(g5,g-4)
    c: DistanceY(g0,g-4) = 0.05
    c: DistanceY(g-6,g3) = 0.05
    c: DistanceX(g-5,g4) = 0.05
    c: DistanceX(g1,g-8) = 0.05
    c: Coincident(g6,g1)
    c: Coincident(g6,g-8)
    c: Coincident(g7,g4)
    c: Coincident(g7,g-5)
    c: Horizontal(g7)
    c: Horizontal(g6)
FEATURE [PartDesign::Pad] Pad149
  Direction = (0,0,-1)
  Length = 0.25
  Length2 = 10
  Profile = -> Sketch232
  ReferenceAxis = -> Sketch232 [N_Axis]
  Refine = true
  Suppressed = false
  Type = 0
FEATURE [Sketcher::SketchObject] Sketch233
  ArcFitTolerance = 1e-06
  AttachmentSupport = -> [Pad149]
  ExternalGeometry = -> [Pad149]
  FullyConstrained = true
  MakeInternals = false
  MapMode = 5
  Placement = pos=(0,0,-1.75) rot=(1,0,0;3.14159rad)
  sketch-geometry (8):
    g0: LineSegment StartX=3.375 StartY=-3.3 StartZ=0 EndX=3.64526 EndY=-4.71914 EndZ=0
    g1: LineSegment StartX=3.64526 StartY=-4.71914 StartZ=0 EndX=4.25474 EndY=-4.71914 EndZ=0
    g2: LineSegment StartX=4.25474 StartY=-4.71914 StartZ=0 EndX=4.525 EndY=-3.3 EndZ=0
    g3: LineSegment StartX=4.525 StartY=-3.3 StartZ=0 EndX=4.27132 EndY=-2.15 EndZ=0
    g4: LineSegment StartX=4.27132 StartY=-2.15 StartZ=0 EndX=3.62868 EndY=-2.15 EndZ=0
    g5: LineSegment StartX=3.62868 StartY=-2.15 StartZ=0 EndX=3.375 EndY=-3.3 EndZ=0
    g6: LineSegment [constr] StartX=3.375 StartY=-3.3 StartZ=0 EndX=3.075 EndY=-3.3 EndZ=0
    g7: LineSegment [constr] StartX=4.525 StartY=-3.3 StartZ=0 EndX=4.825 EndY=-3.3 EndZ=0
  constraints (22):
    c: Coincident(g1,g0)
    c: Horizontal(g1)
    c: Coincident(g2,g1)
    c: Coincident(g3,g2)
    c: Coincident(g4,g3)
    c: Horizontal(g4)
    c: Coincident(g5,g4)
    c: Coincident(g5,g0)
    c: DistanceY(g4,g-8) = 0.3
    c: DistanceY(g-6,g0) = 0.3
    c: Parallel(g5,g-7)
    c: Parallel(g3,g-3)
    c: Parallel(g2,g-4)
    c: Parallel(g0,g-6)
    c: Coincident(g6,g0)
    c: Coincident(g6,g-7)
    c: Coincident(g7,g2)
    c: Coincident(g7,g-4)
    c: Horizontal(g6)
    c: Horizontal(g7)
    c: DistanceX(g6,g6) = 0.3
    c: DistanceX(g7,g7) = 0.3
FEATURE [PartDesign::Pad] Pad150
  BaseFeature = -> Pad149
  Direction = (0,0,-1)
  Length = 0.25
  Length2 = 10
  Profile = -> Sketch233
  ReferenceAxis = -> Sketch233 [N_Axis]
  Refine = true
  Suppressed = false
  Type = 0
FEATURE [PartDesign::Body] Body011  label="Forehead"
  AllowCompound = false
  Group = -> [Binder005,Sketch232,Pad149,Sketch233,Pad150]
  Origin = -> Origin012
  Tip = -> Pad150
FEATURE [PartDesign::SubShapeBinder] Binder006
  BindCopyOnChange = 0
  BindMode = 2
  ClaimChildren = false
  Context = -> Part [Body012.Binder006.]
  Fuse = false
  MakeFace = true
  OffsetFill = false
  OffsetIntersection = false
  OffsetJoinType = 0
  OffsetOpenResult = false
  PartialLoad = false
  Refine = true
  Relative = true
  _Version = 2
FEATURE [Sketcher::SketchObject] Sketch234
  ArcFitTolerance = 1e-06
  AttachmentSupport = -> [Binder006]
  ExternalGeometry = -> [Binder006]
  FullyConstrained = true
  MakeInternals = false
  MapMode = 5
  Placement = pos=(0,0,0) rot=(1,0,0;3.14159rad)
  sketch-geometry (14):
    g0: LineSegment StartX=1.3 StartY=-5.3 StartZ=0 EndX=6.6 EndY=-5.3 EndZ=0
    g1: LineSegment StartX=6.6 StartY=-5.3 StartZ=0 EndX=6.6 EndY=-6.85 EndZ=0
    g2: LineSegment StartX=6.6 StartY=-6.85 StartZ=0 EndX=5.47268 EndY=-6.85 EndZ=0
    g3: LineSegment StartX=5.47268 StartY=-6.85 StartZ=0 EndX=4.62268 EndY=-7.31934 EndZ=0
    g4: LineSegment StartX=4.62268 StartY=-7.31934 StartZ=0 EndX=4.375 EndY=-7.31934 EndZ=0
    g5: LineSegment StartX=4.375 StartY=-7.31934 StartZ=0 EndX=4.375 EndY=-5.71934 EndZ=0
    g6: LineSegment StartX=4.375 StartY=-5.71934 StartZ=0 EndX=3.525 EndY=-5.71934 EndZ=0
    g7: LineSegment StartX=3.525 StartY=-5.71934 StartZ=0 EndX=3.525 EndY=-7.31934 EndZ=0
    g8: LineSegment StartX=3.525 StartY=-7.31934 StartZ=0 EndX=3.27732 EndY=-7.31934 EndZ=0
    g9: LineSegment StartX=3.27732 StartY=-7.31934 StartZ=0 EndX=2.42732 EndY=-6.85 EndZ=0
    g10: LineSegment StartX=2.42732 StartY=-6.85 StartZ=0 EndX=1.3 EndY=-6.85 EndZ=0
    g11: LineSegment StartX=1.3 StartY=-6.85 StartZ=0 EndX=1.3 EndY=-5.3 EndZ=0
    g12: LineSegment [constr] StartX=2.42732 StartY=-6.9 StartZ=0 EndX=2.42732 EndY=-6.85 EndZ=0
    g13: LineSegment [constr] StartX=5.47268 StartY=-6.9 StartZ=0 EndX=5.47268 EndY=-6.85 EndZ=0
  constraints (40):
    c: Horizontal(g0)
    c: Coincident(g1,g0)
    c: Vertical(g1)
    c: Coincident(g2,g1)
    c: Horizontal(g2)
    c: Coincident(g3,g2)
    c: Coincident(g4,g3)
    c: Horizontal(g4)
    c: Coincident(g5,g4)
    c: Vertical(g5)
    c: Coincident(g6,g5)
    c: Horizontal(g6)
    c: Coincident(g7,g6)
    c: Vertical(g7)
    c: Coincident(g8,g7)
    c: Horizontal(g8)
    c: Coincident(g9,g8)
    c: Coincident(g10,g9)
    c: Horizontal(g10)
    c: Coincident(g11,g10)
    c: Coincident(g11,g0)
    c: Vertical(g11)
    c: DistanceX(g-10,g0) = 0.3
    c: DistanceX(g0,g-3) = 0.3
    c: DistanceY(g0,g-3) = 0.1
    c: DistanceY(g-4,g1) = 0.05
    c: Parallel(g3,g-5)
    c: Parallel(g9,g-13)
    c: DistanceY(g-12,g7) = 0.05
    c: DistanceY(g-7,g4) = 0.05
    c: DistanceX(g-7,g4) = 0.05
    c: DistanceX(g7,g-12) = 0.05
    c: DistanceY(g-14,g10) = 0.05
    c: Coincident(g12,g-14)
    c: Coincident(g12,g9)
    c: Vertical(g12)
    c: Coincident(g13,g-5)
    c: Coincident(g13,g2)
    c: Vertical(g13)
    c: DistanceY(g-8,g5) = 0.05
FEATURE [PartDesign::Pad] Pad151
  Direction = (0,0,-1)
  Length = 1
  Length2 = 10
  Profile = -> Sketch234
  ReferenceAxis = -> Sketch234 [N_Axis]
  Refine = true
  Suppressed = false
  Type = 0
FEATURE [Sketcher::SketchObject] Sketch235
  ArcFitTolerance = 1e-06
  AttachmentSupport = -> [Pad151]
  ExternalGeometry = -> [Pad151]
  FullyConstrained = true
  MakeInternals = false
  MapMode = 5
  Placement = pos=(0,5.3,0) rot=(1,0,0;1.5708rad)
  sketch-geometry (4):
    g0: LineSegment StartX=1.3 StartY=-0.2 StartZ=0 EndX=1.3 EndY=-1 EndZ=0
    g1: LineSegment StartX=1.3 StartY=-1 StartZ=0 EndX=6.6 EndY=-1 EndZ=0
    g2: LineSegment StartX=6.6 StartY=-1 StartZ=0 EndX=6.6 EndY=-0.2 EndZ=0
    g3: ArcOfCircle CenterX=3.95 CenterY=3.78906 CenterZ=0 NormalX=0 NormalY=0 NormalZ=1 AngleXU=0 Radius=4.78906 StartAngle=4.12602 EndAngle=5.29876
  constraints (11):
    c: PointOnObject(g0,g-5)
    c: Coincident(g0,g-5)
    c: Coincident(g1,g0)
    c: Coincident(g1,g-4)
    c: Coincident(g2,g1)
    c: PointOnObject(g2,g-4)
    c: DistanceY(g0,g-5) = 0.2
    c: DistanceY(g2,g-4) = 0.2
    c: Coincident(g3,g2)
    c: Coincident(g3,g0)
    c: Tangent(g3,g1)
FEATURE [PartDesign::Pocket] Pocket108
  BaseFeature = -> Pad151
  Direction = (0,1,-2e-16)
  Length = 5
  Length2 = 5
  Profile = -> Sketch235
  ReferenceAxis = -> Sketch235 [N_Axis]
  Refine = true
  Suppressed = false
  Type = 0
FEATURE [PartDesign::Body] Body012  label="Eyes"
  AllowCompound = false
  Group = -> [Binder006,Sketch234,Pad151,Sketch235,Pocket108]
  Origin = -> Origin013
  Tip = -> Pocket108
FEATURE [PartDesign::SubShapeBinder] Binder007
  BindCopyOnChange = 0
  BindMode = 2
  ClaimChildren = false
  Context = -> Part [Body013.Binder007.]
  Fuse = false
  MakeFace = true
  OffsetFill = false
  OffsetIntersection = false
  OffsetJoinType = 0
  OffsetOpenResult = false
  PartialLoad = false
  Refine = true
  Relative = true
  _Version = 2
FEATURE [Sketcher::SketchObject] Sketch236
  ArcFitTolerance = 1e-06
  AttachmentSupport = -> [Binder007]
  ExternalGeometry = -> [Binder007]
  FullyConstrained = true
  MakeInternals = false
  MapMode = 5
  Placement = pos=(0,0,-1) rot=(1,0,0;3.14159rad)
  sketch-geometry (4):
    g0: LineSegment StartX=3.2 StartY=-7.66934 StartZ=0 EndX=3.2 EndY=-9.79934 EndZ=0
    g1: LineSegment StartX=3.2 StartY=-9.79934 StartZ=0 EndX=4.7 EndY=-9.79934 EndZ=0
    g2: LineSegment StartX=4.7 StartY=-9.79934 StartZ=0 EndX=4.7 EndY=-7.66934 EndZ=0
    g3: LineSegment StartX=4.7 StartY=-7.66934 StartZ=0 EndX=3.2 EndY=-7.66934 EndZ=0
  constraints (11):
    c: Coincident(g0,g1)
    c: Coincident(g1,g2)
    c: Coincident(g2,g3)
    c: Coincident(g3,g0)
    c: Vertical(g0)
    c: Vertical(g2)
    c: Horizontal(g1)
    c: Horizontal(g3)
    c: Coincident(g0,g-4)
    c: PointOnObject(g-6,g2)
    c: DistanceY(g0,g0) = 2.13
FEATURE [PartDesign::Pad] Pad152
  Direction = (0,0,-1)
  Length = 1
  Length2 = 10
  Profile = -> Sketch236
  ReferenceAxis = -> Sketch236 [N_Axis]
  Refine = true
  Suppressed = false
  Type = 0
FEATURE [Sketcher::SketchObject] Sketch237
  ArcFitTolerance = 1e-06
  AttachmentSupport = -> [Pad152]
  ExternalGeometry = -> [Pad152]
  FullyConstrained = true
  MakeInternals = false
  MapMode = 5
  Placement = pos=(3.2,0,0) rot=(0.57735,-0.57735,-0.57735;2.0944rad)
  sketch-geometry (3):
    g0: LineSegment StartX=-9.79934 StartY=-2 StartZ=0 EndX=-7.66934 EndY=-1.5 EndZ=0
    g1: LineSegment StartX=-7.66934 StartY=-1.5 StartZ=0 EndX=-7.66934 EndY=-2 EndZ=0
    g2: LineSegment StartX=-7.66934 StartY=-2 StartZ=0 EndX=-9.79934 EndY=-2 EndZ=0
  constraints (7):
    c: Coincident(g0,g-4)
    c: PointOnObject(g0,g-3)
    c: Coincident(g1,g0)
    c: Coincident(g1,g-4)
    c: Coincident(g2,g1)
    c: Coincident(g2,g0)
    c: DistanceY(g1,g1) = 0.5
FEATURE [PartDesign::Pocket] Pocket109
  BaseFeature = -> Pad152
  Direction = (1,0,0)
  Length = 5
  Length2 = 5
  Profile = -> Sketch237
  ReferenceAxis = -> Sketch237 [N_Axis]
  Refine = true
  Suppressed = false
  Type = 0
FEATURE [PartDesign::Body] Body013  label="Chin"
  AllowCompound = false
  Group = -> [Binder007,Sketch236,Pad152,Sketch237,Pocket109]
  Origin = -> Origin014
  Tip = -> Pocket109
FEATURE [PartDesign::Pad] Pad184
  BaseFeature = -> Pocket107
  Direction = (1,0,0)
  Length = 0.05
  Length2 = 10
  Profile = -> Pocket107 [Face67]
  Refine = true
  Suppressed = false
  Type = 0
FEATURE [PartDesign::Pad] Pad185
  BaseFeature = -> Pad184
  Direction = (-1,0,0)
  Length = 0.05
  Length2 = 10
  Profile = -> Pad184 [Face66]
  Refine = true
  Suppressed = false
  Type = 0
FEATURE [PartDesign::Body] Body010  label="Main_Head"
  AllowCompound = false
  Group = -> [Sketch213,Pad137,Sketch214,Pad138,Sketch215,Pad139,Pad140,Sketch216,Pad141,Sketch217,Pad142,Chamfer003,Sketch218,Pocket098,Sketch219,Pad143,Sketch220,Pad144,Sketch221,Pocket099,Sketch222,Pad145,Sketch223,Pocket100,Sketch224,Pocket101,Sketch225,Pocket102,Sketch226,Pad146,Sketch227,Pocket103,Sketch228,Pad147,Sketch229,Pocket104,Pocket105,Pocket106,Sketch230,Pad148,Sketch231,Pocket107,Pad184,Pad185,+4 more]
  Origin = -> Origin011
  Tip = -> Chamfer005
PROVENANCE & LICENSES
A FreeCAD (.FCStd) document from a public repository crawl; recipes are the document's own serialized feature recipes (and, for linked parts, companion documents' recipes).
License: as declared in the source repository (recorded in the dataset sidecar).
